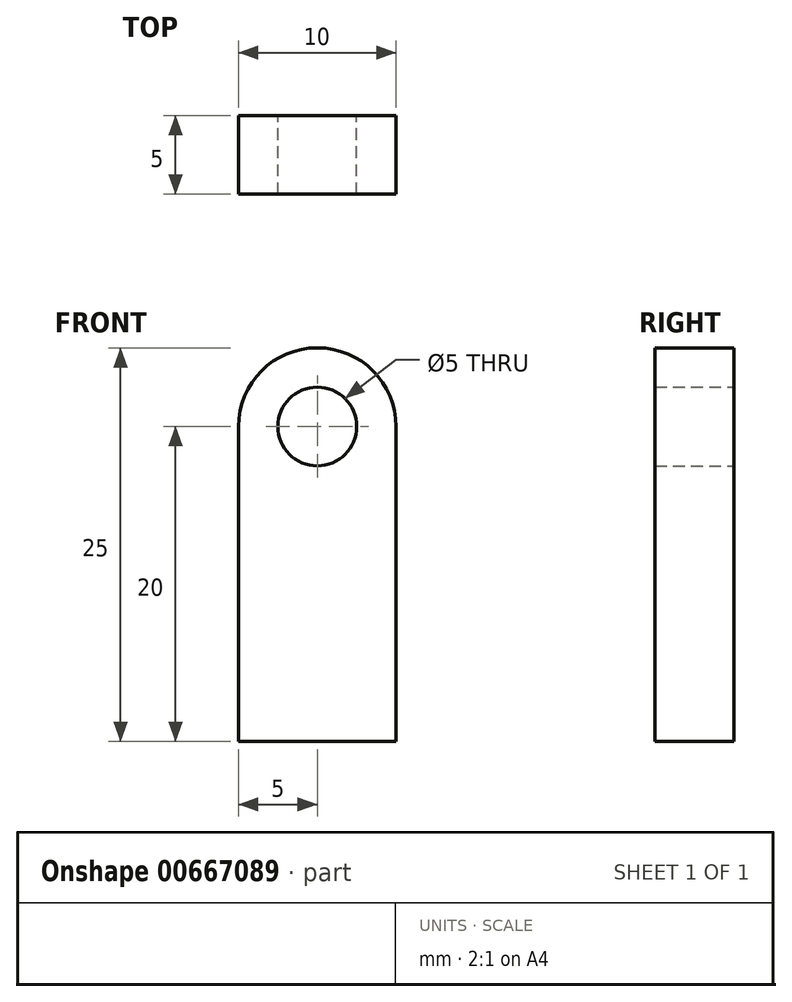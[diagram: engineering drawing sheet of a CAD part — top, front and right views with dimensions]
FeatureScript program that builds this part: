
annotation { "Feature Type Name" : "Feature", "Feature Type Description" : "" }
export const myFeature = defineFeature(function(context is Context, id is Id, definition is map)
    precondition{}
    {
        {
            var Q0;
            Q0=qCreatedBy(makeId("Front.planeOp"),FACE);
            var sketch = newSketch(context, id + "F0", { "sketchPlane" : qUnion([Q0])});
            skArc(sketch, "E0", {"start": v(5, 0) * mm, "mid": v(0, 5) * mm, "end": v(-5, 0) * mm});
            skCircle(sketch, "E1", {"center": v(0, 0) * mm, "radius": 2.5 * mm});
            skLineSegment(sketch, "E2.bottom", {"start": v(-5, 0) * mm, "end": v(5, 0) * mm});
            skLineSegment(sketch, "E2.top", {"start": v(-5, -20) * mm, "end": v(5, -20) * mm});
            skLineSegment(sketch, "E2.left", {"start": v(-5, 0) * mm, "end": v(-5, -20) * mm});
            skLineSegment(sketch, "E2.right", {"start": v(5, 0) * mm, "end": v(5, -20) * mm});
            skSolve(sketch);
        }
        {
            var Q0;
            Q0=makeQuery(id+"F0.imprint","IMPRINT",FACE,{"disambiguationData":[TD([[makeQuery(id+"F0.imprint","IMPRINT",EDGE,{"derivedFrom":sQuery(id+"F0.wireOp",EDGE,"E2.top")}),1.0]])]});
            var Q1;
            {var subQ0=sQuery(id+"F0.wireOp",EDGE,"E0");Q1=makeQuery(id+"F0.imprint","IMPRINT",FACE,{"disambiguationData":[TD([[makeQuery(id+"F0.imprint","IMPRINT",EDGE,{"derivedFrom":subQ0}),1.0]])]});}
            extrude(context, id + "F1", {"entities" : qUnion([Q0, Q1]), "endBound" : BoundingType.SYMMETRIC, "depth" : 5 * mm, "offsetDistance" : 25 * mm});
        }
    });
